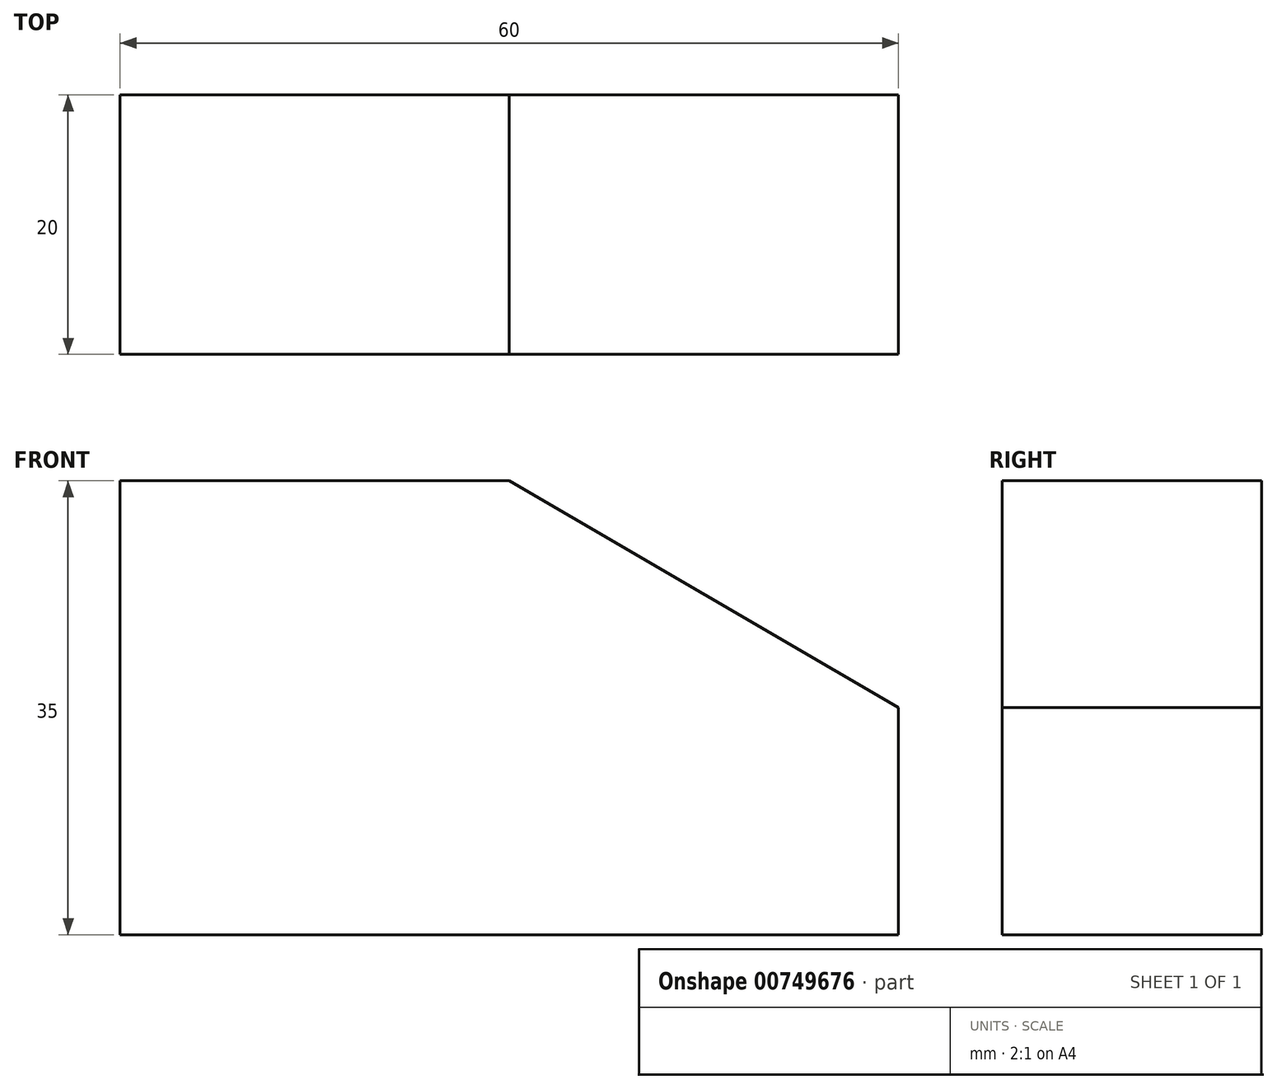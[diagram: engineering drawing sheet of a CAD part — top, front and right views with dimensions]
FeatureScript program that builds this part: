
annotation { "Feature Type Name" : "Feature", "Feature Type Description" : "" }
export const myFeature = defineFeature(function(context is Context, id is Id, definition is map)
    precondition{}
    {
        {
            var Q0;
            Q0=qCreatedBy(makeId("Front.planeOp"),FACE);
            var sketch = newSketch(context, id + "F0", { "sketchPlane" : qUnion([Q0])});
            skLineSegment(sketch, "E0.bottom", {"start": v(-60, 35) * mm, "end": v(-30, 35) * mm});
            skLineSegment(sketch, "E0.top", {"start": v(-60, 0) * mm, "end": v(0, 0) * mm});
            skLineSegment(sketch, "E0.left", {"start": v(-60, 35) * mm, "end": v(-60, 0) * mm});
            skLineSegment(sketch, "E0.right", {"start": v(0, 17.5) * mm, "end": v(0, 0) * mm});
            skLineSegment(sketch, "E1", {"start": v(-30, 35) * mm, "end": v(0, 17.5) * mm});
            skLineSegment(sketch, "E2", {"start": v(-30, 35) * mm, "end": v(0, 35) * mm, "construction": true});
            skLineSegment(sketch, "E3", {"start": v(0, 35) * mm, "end": v(0, 17.5) * mm, "construction": true});
            skSolve(sketch);
        }
        {
            var Q0;
            Q0 = qSketchRegion(id + "F0", true);
            extrude(context, id + "F1", {"entities" : qUnion([Q0]), "depth" : 20 * mm, "offsetDistance" : 25 * mm});
        }
    });
